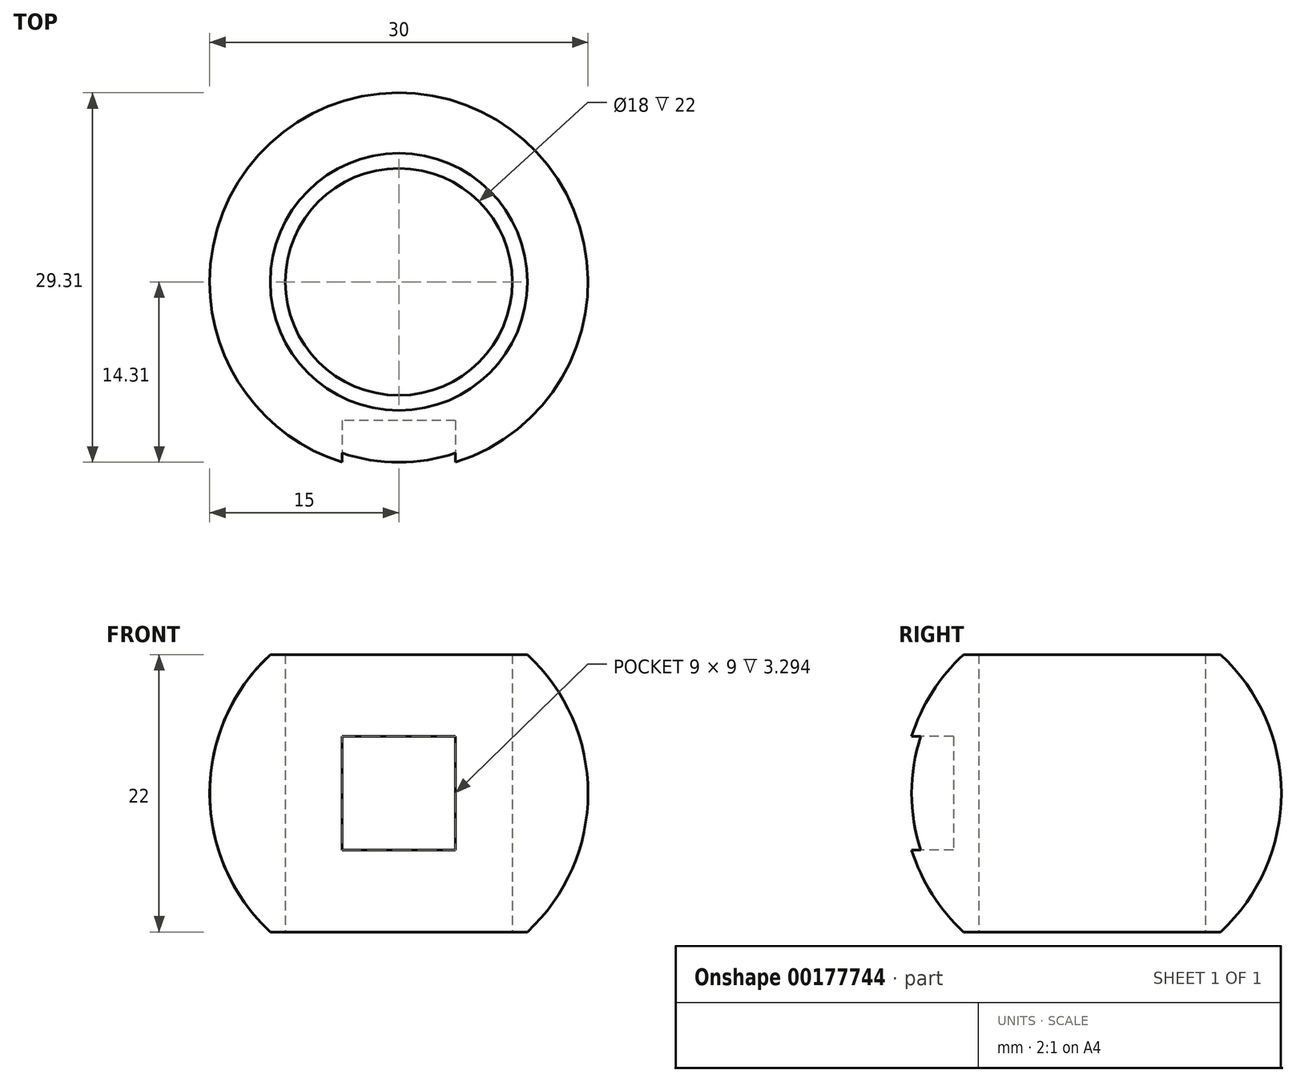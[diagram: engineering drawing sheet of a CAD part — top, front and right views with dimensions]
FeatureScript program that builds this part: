
annotation { "Feature Type Name" : "Feature", "Feature Type Description" : "" }
export const myFeature = defineFeature(function(context is Context, id is Id, definition is map)
    precondition{}
    {
        {
            var Q0;
            Q0=qCreatedBy(makeId("Front.planeOp"),FACE);
            var sketch = newSketch(context, id + "F0", { "sketchPlane" : qUnion([Q0])});
            skArc(sketch, "E0", {"start": v(9, -12) * mm, "mid": v(15, 0) * mm, "end": v(9, 12) * mm});
            skLineSegment(sketch, "E1", {"start": v(9, 12) * mm, "end": v(9, -12) * mm});
            skPoint(sketch, "E2.orphan", {"position": v(0, -15) * mm});
            skLineSegment(sketch, "E3", {"start": v(0, 0) * mm, "end": v(0, 25.55) * mm, "construction": true});
            skSolve(sketch);
        }
        {
            var Q0;
            Q0 = qSketchRegion(id + "F0", true);
            var Q1;
            Q1=sQuery(id+"F0.wireOp",EDGE,"E3");
            revolve(context, id + "F1", {"entities" : qUnion([Q0]), "axis" : qUnion([Q1]), "revolveType" : RevolveType.FULL});
        }
        {
            var Q0;
            Q0=qCreatedBy(makeId("Front.planeOp"),FACE);
            cPlane(context, id + "F2", {"entities" : qUnion([Q0]), "cplaneType" : CPlaneType.OFFSET, "offset" : 15 * mm, "width" : 150 * mm, "height" : 150 * mm});
        }
        {
            var Q0;
            Q0=qCreatedBy(id+"F2.planeOp",FACE);
            var sketch = newSketch(context, id + "F3", { "sketchPlane" : qUnion([Q0])});
            skLineSegment(sketch, "E4.bottom", {"start": v(4.5, 4.5) * mm, "end": v(-4.5, 4.5) * mm});
            skLineSegment(sketch, "E4.top", {"start": v(4.5, -4.5) * mm, "end": v(-4.5, -4.5) * mm});
            skLineSegment(sketch, "E4.left", {"start": v(4.5, 4.5) * mm, "end": v(4.5, -4.5) * mm});
            skLineSegment(sketch, "E4.right", {"start": v(-4.5, 4.5) * mm, "end": v(-4.5, -4.5) * mm});
            skPoint(sketch, "E4.middle", {"position": v(0, 0) * mm});
            skSolve(sketch);
        }
        {
            var Q0;
            Q0 = qSketchRegion(id + "F3", true);
            extrude(context, id + "F4", {"entities" : qUnion([Q0]), "operationType" : NewBodyOperationType.REMOVE, "oppositeDirection" : true, "depth" : 4 * mm});
        }
        {
            var Q0;
            Q0=qCreatedBy(makeId("Front.planeOp"),FACE);
            var sketch = newSketch(context, id + "F5", { "sketchPlane" : qUnion([Q0])});
            skLineSegment(sketch, "E5", {"start": v(0, 0) * mm, "end": v(-55.48, 0) * mm, "construction": true});
            skLineSegment(sketch, "E6.bottom", {"start": v(-20.47, 11) * mm, "end": v(17.6, 11) * mm});
            skLineSegment(sketch, "E6.top", {"start": v(-20.47, 23.24) * mm, "end": v(17.6, 23.24) * mm});
            skLineSegment(sketch, "E6.left", {"start": v(-20.47, 11) * mm, "end": v(-20.47, 23.24) * mm});
            skLineSegment(sketch, "E6.right", {"start": v(17.6, 11) * mm, "end": v(17.6, 23.24) * mm});
            skLineSegment(sketch, "E7.MirrorCS", {"start": v(17.6, -11) * mm, "end": v(17.6, -23.24) * mm});
            skLineSegment(sketch, "E8.MirrorCS", {"start": v(-20.47, -23.24) * mm, "end": v(17.6, -23.24) * mm});
            skLineSegment(sketch, "E9.MirrorCS", {"start": v(-20.47, -11) * mm, "end": v(17.6, -11) * mm});
            skLineSegment(sketch, "E10.MirrorCS", {"start": v(-20.47, -11) * mm, "end": v(-20.47, -23.24) * mm});
            skSolve(sketch);
        }
        {
            var Q0;
            Q0 = qSketchRegion(id + "F5", true);
            extrude(context, id + "F6", {"entities" : qUnion([Q0]), "operationType" : NewBodyOperationType.REMOVE, "oppositeDirection" : true, "depth" : 25 * mm, "hasSecondDirection" : true, "secondDirectionOppositeDirection" : false, "secondDirectionDepth" : 25 * mm});
        }
    });
